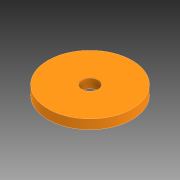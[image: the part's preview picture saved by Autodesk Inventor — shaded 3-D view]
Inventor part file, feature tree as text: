
AUTODESK INVENTOR PART (.ipt)
format: ipt  version: 2021 (Build 250183000, 183)  size: 81,920 bytes
history: native  units: mm
features: extrude x1, sketch x1
ambient origin geometry x8: Origin, YZ Plane, XZ Plane, XY Plane, X Axis, Y Axis, Z Axis, Center Point
bodies: Solid1 (feature_tree)
feature tree (2):
  extrude  "Extrusion1"  Depth=2.0mm
  sketch  "Sketch1"  dims[d0=18.0mm d1=3.5mm d2=2.0mm d3=0.0mm]
